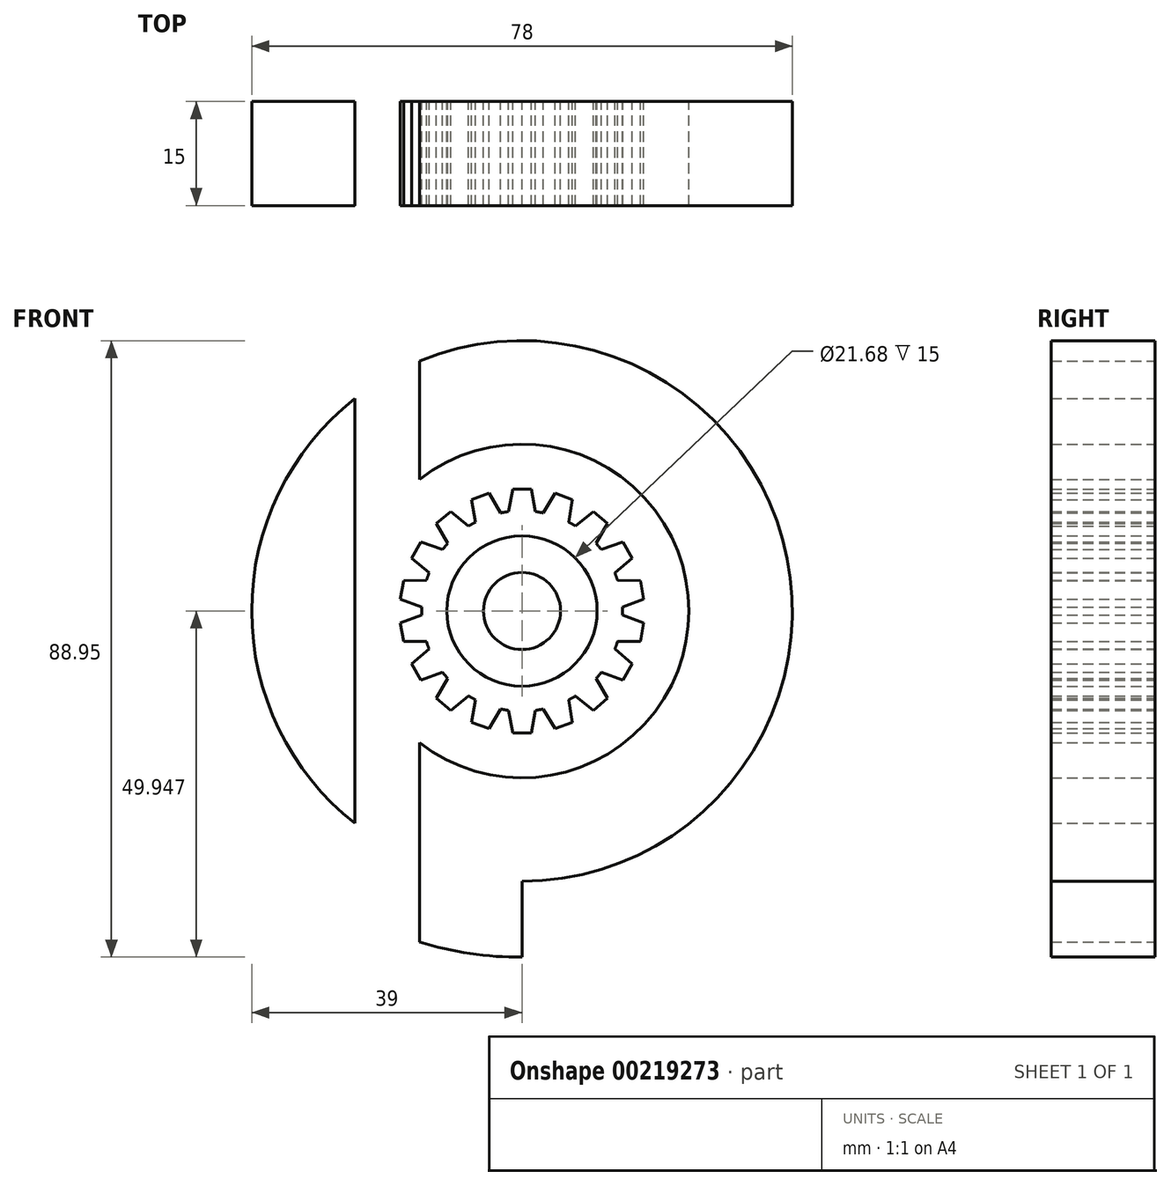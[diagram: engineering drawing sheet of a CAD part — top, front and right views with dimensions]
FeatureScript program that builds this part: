
annotation { "Feature Type Name" : "Feature", "Feature Type Description" : "" }
export const myFeature = defineFeature(function(context is Context, id is Id, definition is map)
    precondition{}
    {
        {
            var Q0;
            Q0=qCreatedBy(makeId("Front.planeOp"),FACE);
            var sketch = newSketch(context, id + "F0", { "sketchPlane" : qUnion([Q0])});
            skPoint(sketch, "E0", {"position": v(0, 44.46) * mm});
            skPoint(sketch, "E1", {"position": v(38.94, 0) * mm});
            skArc(sketch, "E2", {"start": v(-24.14, 36.12) * mm, "mid": v(-39, 5.49) * mm, "end": v(-24.14, -25.15) * mm});
            skArc(sketch, "E3", {"start": v(-14.8, -13.49) * mm, "mid": v(24.07, 5.49) * mm, "end": v(-14.8, 24.46) * mm});
            skCircle(sketch, "E4", {"center": v(0, 5.49) * mm, "radius": 10.84 * mm});
            skArc(sketch, "E5", {"start": v(-14.46, 6.06) * mm, "mid": v(-14.48, 5.49) * mm, "end": v(-14.46, 4.91) * mm});
            skCircle(sketch, "E6", {"center": v(0, 5.49) * mm, "radius": 5.57 * mm});
            skLineSegment(sketch, "E7.left", {"start": v(-24.14, 36.12) * mm, "end": v(-24.14, -25.15) * mm});
            skLineSegment(sketch, "E7.right", {"start": v(-14.8, 41.57) * mm, "end": v(-14.8, 24.46) * mm});
            skLineSegment(sketch, "E8.trimOffspring", {"start": v(-14.8, -30.6) * mm, "end": v(-14.8, -30.6) * mm});
            skLineSegment(sketch, "E9.trimOffspring", {"start": v(-14.8, -13.49) * mm, "end": v(-14.8, -30.6) * mm});
            skLineSegment(sketch, "E10", {"start": v(-1.95, 19.83) * mm, "end": v(-1.34, 23.08) * mm});
            skLineSegment(sketch, "E11", {"start": v(-1.34, 23.08) * mm, "end": v(1.34, 23.08) * mm});
            skLineSegment(sketch, "E12", {"start": v(1.34, 23.08) * mm, "end": v(1.95, 19.83) * mm});
            skPoint(sketch, "E13", {"position": v(0, 23.08) * mm});
            skLineSegment(sketch, "E14.1.0", {"start": v(3.08, 19.63) * mm, "end": v(4.75, 22.47) * mm});
            skLineSegment(sketch, "E14.1.1", {"start": v(4.75, 22.47) * mm, "end": v(7.28, 21.56) * mm});
            skLineSegment(sketch, "E14.1.2", {"start": v(7.28, 21.56) * mm, "end": v(6.74, 18.3) * mm});
            skLineSegment(sketch, "E14.2.0", {"start": v(7.73, 17.73) * mm, "end": v(10.28, 19.82) * mm});
            skLineSegment(sketch, "E14.2.1", {"start": v(10.28, 19.82) * mm, "end": v(12.33, 18.1) * mm});
            skLineSegment(sketch, "E14.2.2", {"start": v(12.33, 18.1) * mm, "end": v(10.71, 15.22) * mm});
            skLineSegment(sketch, "E14.3.0", {"start": v(11.45, 14.35) * mm, "end": v(14.56, 15.44) * mm});
            skLineSegment(sketch, "E14.3.1", {"start": v(14.56, 15.44) * mm, "end": v(15.9, 13.12) * mm});
            skLineSegment(sketch, "E14.3.2", {"start": v(15.9, 13.12) * mm, "end": v(13.4, 10.97) * mm});
            skLineSegment(sketch, "E14.4.0", {"start": v(13.79, 9.9) * mm, "end": v(17.09, 9.86) * mm});
            skLineSegment(sketch, "E14.4.1", {"start": v(17.09, 9.86) * mm, "end": v(17.55, 7.22) * mm});
            skLineSegment(sketch, "E14.4.2", {"start": v(17.55, 7.22) * mm, "end": v(14.46, 6.06) * mm});
            skLineSegment(sketch, "E14.5.0", {"start": v(14.46, 4.91) * mm, "end": v(17.55, 3.76) * mm});
            skLineSegment(sketch, "E14.5.1", {"start": v(17.55, 3.76) * mm, "end": v(17.09, 1.11) * mm});
            skLineSegment(sketch, "E14.5.2", {"start": v(17.09, 1.11) * mm, "end": v(13.79, 1.08) * mm});
            skLineSegment(sketch, "E14.6.0", {"start": v(13.4, 0) * mm, "end": v(15.9, -2.14) * mm});
            skLineSegment(sketch, "E14.6.1", {"start": v(15.9, -2.14) * mm, "end": v(14.56, -4.47) * mm});
            skLineSegment(sketch, "E14.6.2", {"start": v(14.56, -4.47) * mm, "end": v(11.45, -3.37) * mm});
            skLineSegment(sketch, "E14.7.0", {"start": v(10.71, -4.25) * mm, "end": v(12.33, -7.12) * mm});
            skLineSegment(sketch, "E14.7.1", {"start": v(12.33, -7.12) * mm, "end": v(10.28, -8.85) * mm});
            skLineSegment(sketch, "E14.7.2", {"start": v(10.28, -8.85) * mm, "end": v(7.73, -6.75) * mm});
            skLineSegment(sketch, "E14.8.0", {"start": v(6.74, -7.33) * mm, "end": v(7.28, -10.58) * mm});
            skLineSegment(sketch, "E14.8.1", {"start": v(7.28, -10.58) * mm, "end": v(4.75, -11.5) * mm});
            skLineSegment(sketch, "E14.8.2", {"start": v(4.75, -11.5) * mm, "end": v(3.08, -8.66) * mm});
            skLineSegment(sketch, "E14.anchor1", {"start": v(0, 5.49) * mm, "end": v(-1.95, 19.83) * mm, "construction": true});
            skLineSegment(sketch, "E14.anchor2", {"start": v(0, 5.49) * mm, "end": v(6.74, -7.33) * mm, "construction": true});
            skLineSegment(sketch, "E15.1.0", {"start": v(-1.34, -12.1) * mm, "end": v(-1.95, -8.86) * mm});
            skLineSegment(sketch, "E15.1.1", {"start": v(1.34, -12.1) * mm, "end": v(-1.34, -12.1) * mm});
            skLineSegment(sketch, "E15.1.2", {"start": v(1.95, -8.86) * mm, "end": v(1.34, -12.1) * mm});
            skLineSegment(sketch, "E15.2.0", {"start": v(-7.28, -10.58) * mm, "end": v(-6.74, -7.33) * mm});
            skLineSegment(sketch, "E15.2.1", {"start": v(-4.75, -11.5) * mm, "end": v(-7.28, -10.58) * mm});
            skLineSegment(sketch, "E15.2.2", {"start": v(-3.08, -8.66) * mm, "end": v(-4.75, -11.5) * mm});
            skLineSegment(sketch, "E15.3.0", {"start": v(-12.33, -7.12) * mm, "end": v(-10.71, -4.25) * mm});
            skLineSegment(sketch, "E15.3.1", {"start": v(-10.28, -8.85) * mm, "end": v(-12.33, -7.12) * mm});
            skLineSegment(sketch, "E15.3.2", {"start": v(-7.73, -6.75) * mm, "end": v(-10.28, -8.85) * mm});
            skLineSegment(sketch, "E15.4.0", {"start": v(-15.9, -2.14) * mm, "end": v(-13.4, 0) * mm});
            skLineSegment(sketch, "E15.4.1", {"start": v(-14.56, -4.47) * mm, "end": v(-15.9, -2.14) * mm});
            skLineSegment(sketch, "E15.4.2", {"start": v(-11.45, -3.37) * mm, "end": v(-14.56, -4.47) * mm});
            skLineSegment(sketch, "E15.5.0", {"start": v(-17.55, 3.76) * mm, "end": v(-14.46, 4.91) * mm});
            skLineSegment(sketch, "E15.5.1", {"start": v(-17.09, 1.11) * mm, "end": v(-17.55, 3.76) * mm});
            skLineSegment(sketch, "E15.5.2", {"start": v(-13.79, 1.08) * mm, "end": v(-17.09, 1.11) * mm});
            skLineSegment(sketch, "E15.6.0", {"start": v(-17.09, 9.86) * mm, "end": v(-13.79, 9.9) * mm});
            skLineSegment(sketch, "E15.6.1", {"start": v(-17.55, 7.22) * mm, "end": v(-17.09, 9.86) * mm});
            skLineSegment(sketch, "E15.6.2", {"start": v(-14.46, 6.06) * mm, "end": v(-17.55, 7.22) * mm});
            skLineSegment(sketch, "E15.7.0", {"start": v(-14.56, 15.44) * mm, "end": v(-11.45, 14.35) * mm});
            skLineSegment(sketch, "E15.7.1", {"start": v(-15.9, 13.12) * mm, "end": v(-14.56, 15.44) * mm});
            skLineSegment(sketch, "E15.7.2", {"start": v(-13.4, 10.97) * mm, "end": v(-15.9, 13.12) * mm});
            skLineSegment(sketch, "E15.8.0", {"start": v(-10.28, 19.82) * mm, "end": v(-7.73, 17.73) * mm});
            skLineSegment(sketch, "E15.8.1", {"start": v(-12.33, 18.1) * mm, "end": v(-10.28, 19.82) * mm});
            skLineSegment(sketch, "E15.8.2", {"start": v(-10.71, 15.22) * mm, "end": v(-12.33, 18.1) * mm});
            skLineSegment(sketch, "E15.9.0", {"start": v(-4.75, 22.47) * mm, "end": v(-3.08, 19.63) * mm});
            skLineSegment(sketch, "E15.9.1", {"start": v(-7.28, 21.56) * mm, "end": v(-4.75, 22.47) * mm});
            skLineSegment(sketch, "E15.9.2", {"start": v(-6.74, 18.3) * mm, "end": v(-7.28, 21.56) * mm});
            skLineSegment(sketch, "E15.anchor1", {"start": v(0, 5.49) * mm, "end": v(4.75, -11.5) * mm, "construction": true});
            skLineSegment(sketch, "E15.anchor2", {"start": v(0, 5.49) * mm, "end": v(-4.75, 22.47) * mm, "construction": true});
            skArc(sketch, "E16.trimOffspring", {"start": v(-13.4, 10.97) * mm, "mid": v(-13.6, 10.44) * mm, "end": v(-13.79, 9.9) * mm});
            skArc(sketch, "E17.trimOffspring", {"start": v(-10.71, 15.22) * mm, "mid": v(-11.09, 14.8) * mm, "end": v(-11.45, 14.35) * mm});
            skArc(sketch, "E18.trimOffspring", {"start": v(-6.74, 18.3) * mm, "mid": v(-7.24, 18.02) * mm, "end": v(-7.73, 17.73) * mm});
            skArc(sketch, "E19.trimOffspring", {"start": v(-1.95, 19.83) * mm, "mid": v(-2.93, 19.66) * mm, "end": v(-3.9, 19.43) * mm});
            skArc(sketch, "E20.trimOffspring", {"start": v(3.08, 19.63) * mm, "mid": v(2.51, 19.74) * mm, "end": v(1.95, 19.83) * mm});
            skArc(sketch, "E21.trimOffspring", {"start": v(7.73, 17.73) * mm, "mid": v(7.24, 18.02) * mm, "end": v(6.74, 18.3) * mm});
            skArc(sketch, "E22.trimOffspring", {"start": v(11.45, 14.35) * mm, "mid": v(11.09, 14.8) * mm, "end": v(10.71, 15.22) * mm});
            skArc(sketch, "E23.trimOffspring", {"start": v(13.79, 9.9) * mm, "mid": v(13.6, 10.44) * mm, "end": v(13.4, 10.97) * mm});
            skArc(sketch, "E24.trimOffspring", {"start": v(14.46, 4.91) * mm, "mid": v(14.48, 5.49) * mm, "end": v(14.46, 6.06) * mm});
            skArc(sketch, "E25.trimOffspring", {"start": v(13.4, 0) * mm, "mid": v(13.6, 0.54) * mm, "end": v(13.79, 1.08) * mm});
            skArc(sketch, "E26.trimOffspring", {"start": v(10.71, -4.25) * mm, "mid": v(11.09, -3.82) * mm, "end": v(11.45, -3.37) * mm});
            skArc(sketch, "E27.trimOffspring", {"start": v(6.74, -7.33) * mm, "mid": v(7.24, -7.05) * mm, "end": v(7.73, -6.75) * mm});
            skArc(sketch, "E28.trimOffspring", {"start": v(1.95, -8.86) * mm, "mid": v(2.93, -8.69) * mm, "end": v(3.9, -8.45) * mm});
            skArc(sketch, "E29.trimOffspring", {"start": v(-3.08, -8.66) * mm, "mid": v(-2.51, -8.77) * mm, "end": v(-1.95, -8.86) * mm});
            skArc(sketch, "E30.trimOffspring", {"start": v(-7.73, -6.75) * mm, "mid": v(-7.24, -7.05) * mm, "end": v(-6.74, -7.33) * mm});
            skArc(sketch, "E31.trimOffspring", {"start": v(-11.45, -3.37) * mm, "mid": v(-11.09, -3.82) * mm, "end": v(-10.71, -4.25) * mm});
            skArc(sketch, "E32.trimOffspring", {"start": v(-13.79, 1.08) * mm, "mid": v(-13.6, 0.54) * mm, "end": v(-13.4, 0) * mm});
            skArc(sketch, "E33", {"start": v(0, -33.51) * mm, "mid": v(38.26, 13.03) * mm, "end": v(-14.8, 41.57) * mm});
            skArc(sketch, "E34", {"start": v(-14.8, -42.25) * mm, "mid": v(-7.49, -43.94) * mm, "end": v(0, -44.46) * mm});
            skLineSegment(sketch, "E35", {"start": v(0, -33.51) * mm, "end": v(0, -44.46) * mm});
            skLineSegment(sketch, "E36", {"start": v(-14.8, -30.6) * mm, "end": v(-14.8, -42.25) * mm});
            skSolve(sketch);
        }
        {
            var Q0;
            Q0=makeQuery(id+"F0.imprint","IMPRINT",FACE,{"disambiguationData":[TD([[makeQuery(id+"F0.imprint","IMPRINT",EDGE,{"derivedFrom":sQuery(id+"F0.wireOp",EDGE,"E4")}),-1.0]])]});
            var Q1;
            Q1=makeQuery(id+"F0.imprint","IMPRINT",FACE,{"disambiguationData":[TD([[makeQuery(id+"F0.imprint","IMPRINT",EDGE,{"derivedFrom":sQuery(id+"F0.wireOp",EDGE,"E6")}),1.0]])]});
            extrude(context, id + "F1", {"entities" : qUnion([Q0, Q1]), "depth" : 15 * mm});
        }
        {
            var Q0;
            Q0=makeQuery(id+"F0.imprint","IMPRINT",FACE,{"disambiguationData":[TD([[makeQuery(id+"F0.imprint","IMPRINT",EDGE,{"derivedFrom":sQuery(id+"F0.wireOp",EDGE,"E3")}),-1.0]])]});
            var Q1;
            Q1=makeQuery(id+"F0.imprint","IMPRINT",FACE,{"disambiguationData":[TD([[makeQuery(id+"F0.imprint","IMPRINT",EDGE,{"derivedFrom":sQuery(id+"F0.wireOp",EDGE,"E2")}),1.0]])]});
            extrude(context, id + "F2", {"entities" : qUnion([Q0, Q1]), "depth" : 15 * mm});
        }
    });
